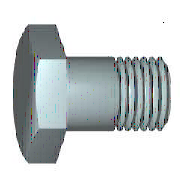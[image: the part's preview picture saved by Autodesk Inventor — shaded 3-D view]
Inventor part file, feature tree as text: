
AUTODESK INVENTOR PART (.ipt)
format: ipt  version: 2020 (Build 240168000, 168)  size: 197,120 bytes
history: native  units: mm (DEFAULTED — no unit token found)
features: sketch x3, extrude x1, chamfer x1, plane x1
ambient origin geometry x7: Origin, YZ Plane, XZ Plane, X Axis, Y Axis, Z Axis, Center Point
bodies: Solid1 (feature_tree), Body (feature_tree)
feature tree (6):
  extrude  "Head"  Depth=7.25mm
  chamfer  "Chamfer1"  Distance=2.829mm
  plane  "Work Plane1"
  sketch  "Sketch1"  dims[d0=9.0mm d1=7.25mm]
  sketch  "Sketch2"  dims[d2=4.0mm]
  sketch  "Sketch4"  dims[d12=90.0deg d3=2.829mm d4=0.0mm d5=30.0deg d21=90.0deg d6=0.429415mm d7=0.429515mm d8=0.0mm d9=0.1001mm d10=6.3mm d11=7.0mm d13=0.429515mm d14=4.0mm d15=7.25mm d16=0.0mm d19=7.0mm d55=45.0deg d57=0.0mm d58=0.0mm]
